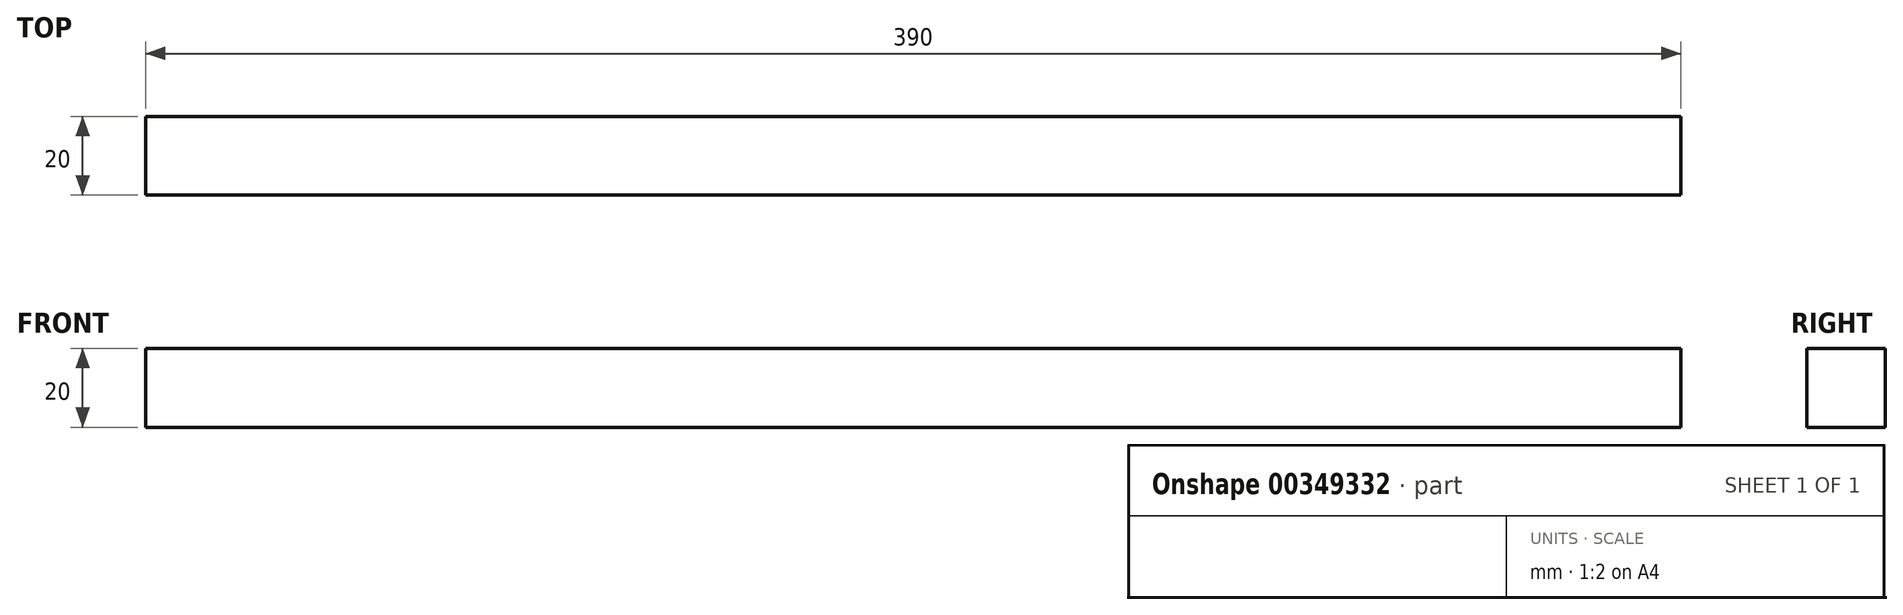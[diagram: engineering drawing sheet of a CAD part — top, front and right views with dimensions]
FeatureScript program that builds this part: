
annotation { "Feature Type Name" : "Feature", "Feature Type Description" : "" }
export const myFeature = defineFeature(function(context is Context, id is Id, definition is map)
    precondition{}
    {
        {
            var Q0;
            Q0=qCreatedBy(makeId("Front.planeOp"),FACE);
            var sketch = newSketch(context, id + "F0", { "sketchPlane" : qUnion([Q0])});
            skLineSegment(sketch, "E0.bottom", {"start": v(-195, 10) * mm, "end": v(195, 10) * mm});
            skLineSegment(sketch, "E0.top", {"start": v(-195, -10) * mm, "end": v(195, -10) * mm});
            skLineSegment(sketch, "E0.left", {"start": v(-195, 10) * mm, "end": v(-195, -10) * mm});
            skLineSegment(sketch, "E0.right", {"start": v(195, 10) * mm, "end": v(195, -10) * mm});
            skPoint(sketch, "E0.middle", {"position": v(0, 0) * mm});
            skSolve(sketch);
        }
        {
            var Q0;
            Q0 = qSketchRegion(id + "F0", true);
            extrude(context, id + "F1", {"entities" : qUnion([Q0]), "endBound" : BoundingType.SYMMETRIC, "depth" : 20 * mm});
        }
    });
